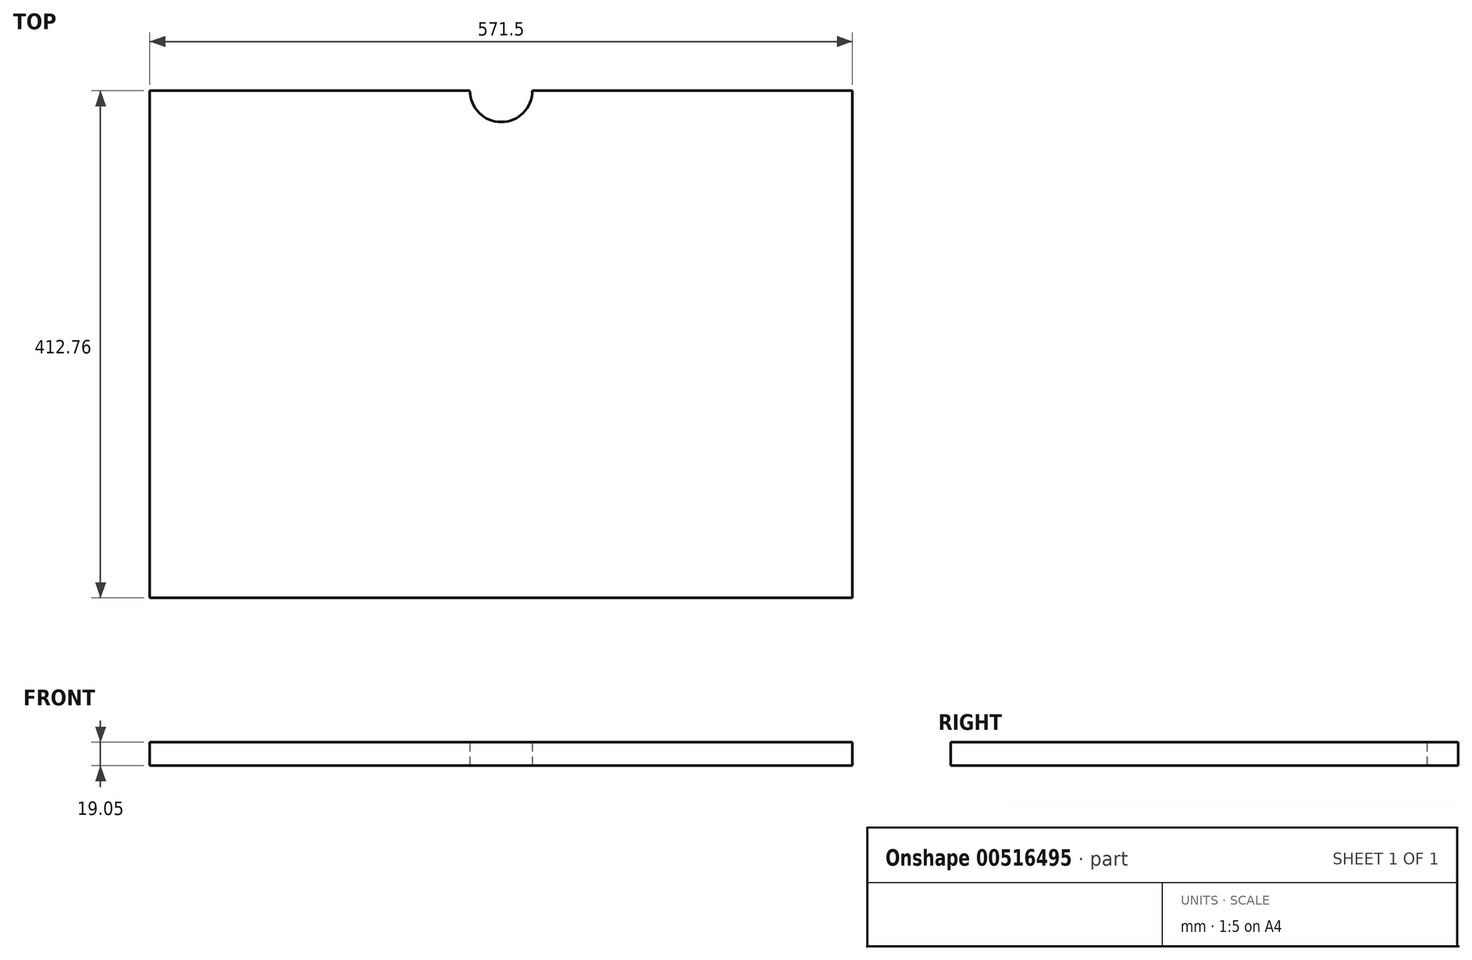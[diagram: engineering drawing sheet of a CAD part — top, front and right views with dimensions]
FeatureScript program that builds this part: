
annotation { "Feature Type Name" : "Feature", "Feature Type Description" : "" }
export const myFeature = defineFeature(function(context is Context, id is Id, definition is map)
    precondition{}
    {
        {
            var Q0;
            Q0=qCreatedBy(makeId("Top.planeOp"),FACE);
            var sketch = newSketch(context, id + "F0", { "sketchPlane" : qUnion([Q0])});
            skLineSegment(sketch, "E0.bottom", {"start": v(285.75, -206.38) * mm, "end": v(-285.75, -206.38) * mm});
            skLineSegment(sketch, "E0.top", {"start": v(285.75, 206.38) * mm, "end": v(-285.75, 206.38) * mm});
            skLineSegment(sketch, "E0.left", {"start": v(285.75, -206.38) * mm, "end": v(285.75, 206.38) * mm});
            skLineSegment(sketch, "E0.right", {"start": v(-285.75, -206.38) * mm, "end": v(-285.75, 206.38) * mm});
            skPoint(sketch, "E0.middle", {"position": v(0, 0) * mm});
            skCircle(sketch, "E1", {"center": v(0, 206.38) * mm, "radius": 25.4 * mm});
            skSolve(sketch);
        }
        {
            var Q0;
            Q0=makeQuery(id+"F0.imprint","IMPRINT",FACE,{"disambiguationData":[TD([[makeQuery(id+"F0.imprint","IMPRINT",EDGE,{"derivedFrom":sQuery(id+"F0.wireOp",EDGE,"E0.bottom")}),-1.0]])]});
            extrude(context, id + "F1", {"entities" : qUnion([Q0]), "depth" : 19.05 * mm, "offsetDistance" : 25.4 * mm});
        }
    });
